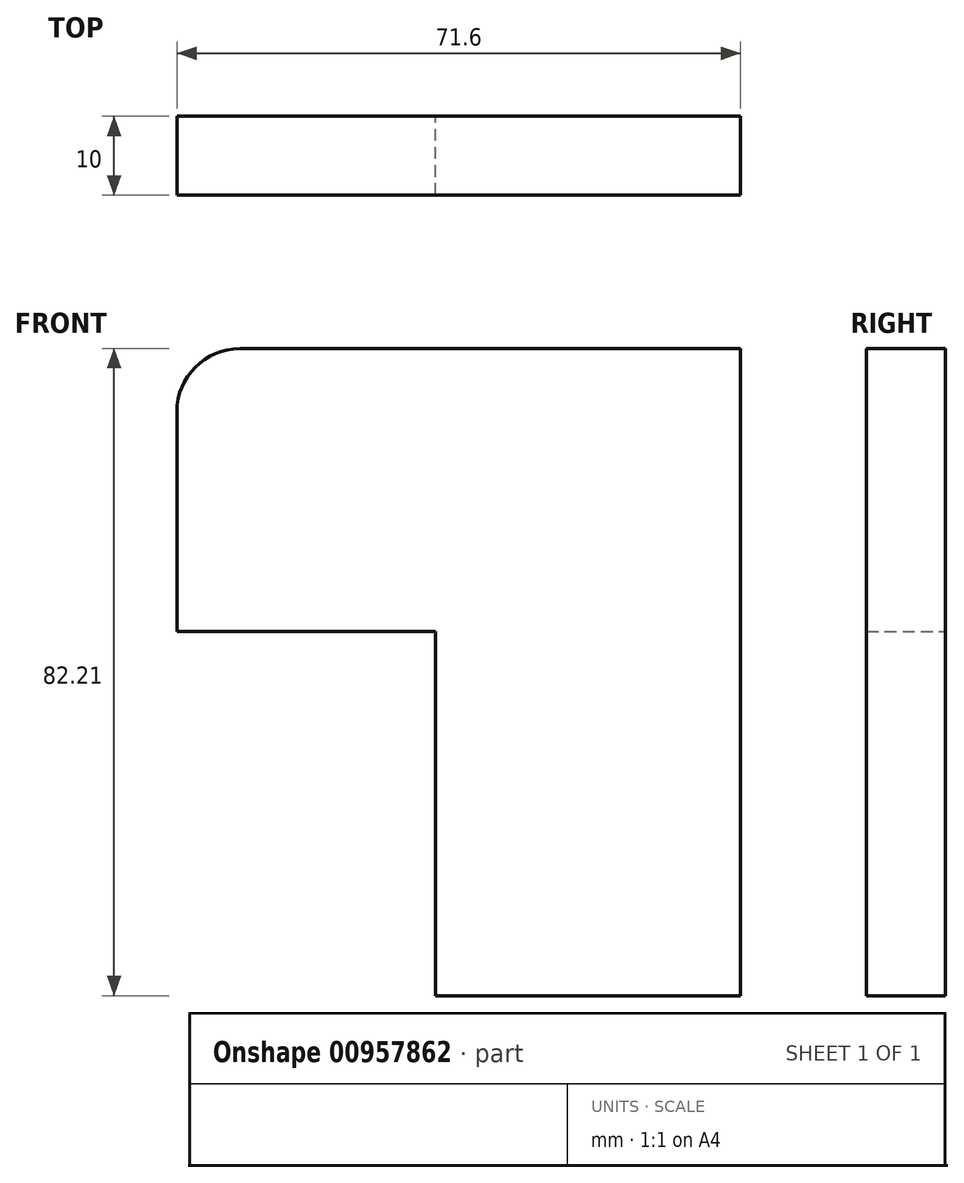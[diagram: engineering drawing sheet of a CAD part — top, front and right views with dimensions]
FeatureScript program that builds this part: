
annotation { "Feature Type Name" : "Feature", "Feature Type Description" : "" }
export const myFeature = defineFeature(function(context is Context, id is Id, definition is map)
    precondition{}
    {
        {
            var Q0;
            Q0=qCreatedBy(makeId("Front.planeOp"),FACE);
            var sketch = newSketch(context, id + "F0", { "sketchPlane" : qUnion([Q0])});
            skLineSegment(sketch, "E0", {"start": v(0, 0) * mm, "end": v(-32.87, 0) * mm});
            skLineSegment(sketch, "E1", {"start": v(-32.87, 0) * mm, "end": v(-32.87, 27.94) * mm});
            skLineSegment(sketch, "E2", {"start": v(-24.87, 35.94) * mm, "end": v(38.73, 35.94) * mm});
            skLineSegment(sketch, "E3", {"start": v(38.73, 35.94) * mm, "end": v(38.73, -46.27) * mm});
            skLineSegment(sketch, "E4", {"start": v(38.73, -46.27) * mm, "end": v(0, -46.27) * mm});
            skLineSegment(sketch, "E5", {"start": v(0, -46.27) * mm, "end": v(0, 0) * mm});
            skPoint(sketch, "E6.visualSharp", {"position": v(-32.87, 35.94) * mm});
            skArc(sketch, "E6.filletArc", {"start": v(-24.87, 35.94) * mm, "mid": v(-30.53, 33.6) * mm, "end": v(-32.87, 27.94) * mm});
            skSolve(sketch);
        }
        {
            var Q0;
            Q0=makeQuery(id+"F0.imprint","IMPRINT",FACE,{"disambiguationData":[TD([[makeQuery(id+"F0.imprint","IMPRINT",EDGE,{"derivedFrom":sQuery(id+"F0.wireOp",EDGE,"E0")}),-1.0]])]});
            extrude(context, id + "F1", {"entities" : qUnion([Q0]), "depth" : 10 * mm, "offsetDistance" : 25 * mm});
        }
    });
